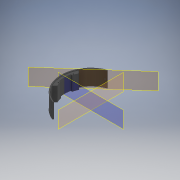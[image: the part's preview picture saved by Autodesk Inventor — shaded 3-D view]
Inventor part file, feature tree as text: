
AUTODESK INVENTOR PART (.ipt)
format: ipt  version: 2020 (Build 240168000, 168)  size: 195,072 bytes
history: native  units: mm
features: sketch x6, other x5, extrude x3, hole x2, chamfer x1, mirror x1
ambient origin geometry x8: Origin, YZ Plane, XZ Plane, XY Plane, X Axis, Y Axis, Z Axis, Center Point
bodies: Body1 (feature_tree)
feature tree (18):
  other  "protect_v2"
  other  "floor_v2.ipt"
  other  "Твердое тело1"
  sketch  "Эскиз4"
  extrude  "Выдавливание1"  Depth=10.0mm
  sketch  "Эскиз5"
  extrude  "Выдавливание2"  Depth=6.0mm
  other  "РабПлоскость1"
  extrude  "Выдавливание3"  Depth=6.0mm
  chamfer  "Фаска1"  Distance=51.15mm
  other  "РабПлоскость2"
  mirror  "Зеркальное отражение1"
  hole  "Отверстие1"  [1 undecoded]
  hole  "Отверстие2"  [1 undecoded]
  sketch  "Эскиз2"
  sketch  "Эскиз7"
  sketch  "Эскиз6"
  sketch  "Эскиз8"
note: 2 required parameter values undecoded (feature->parameter linkage not recoverable at this tier; creation-order binding heuristic only, values carry confidence <= 0.55)
